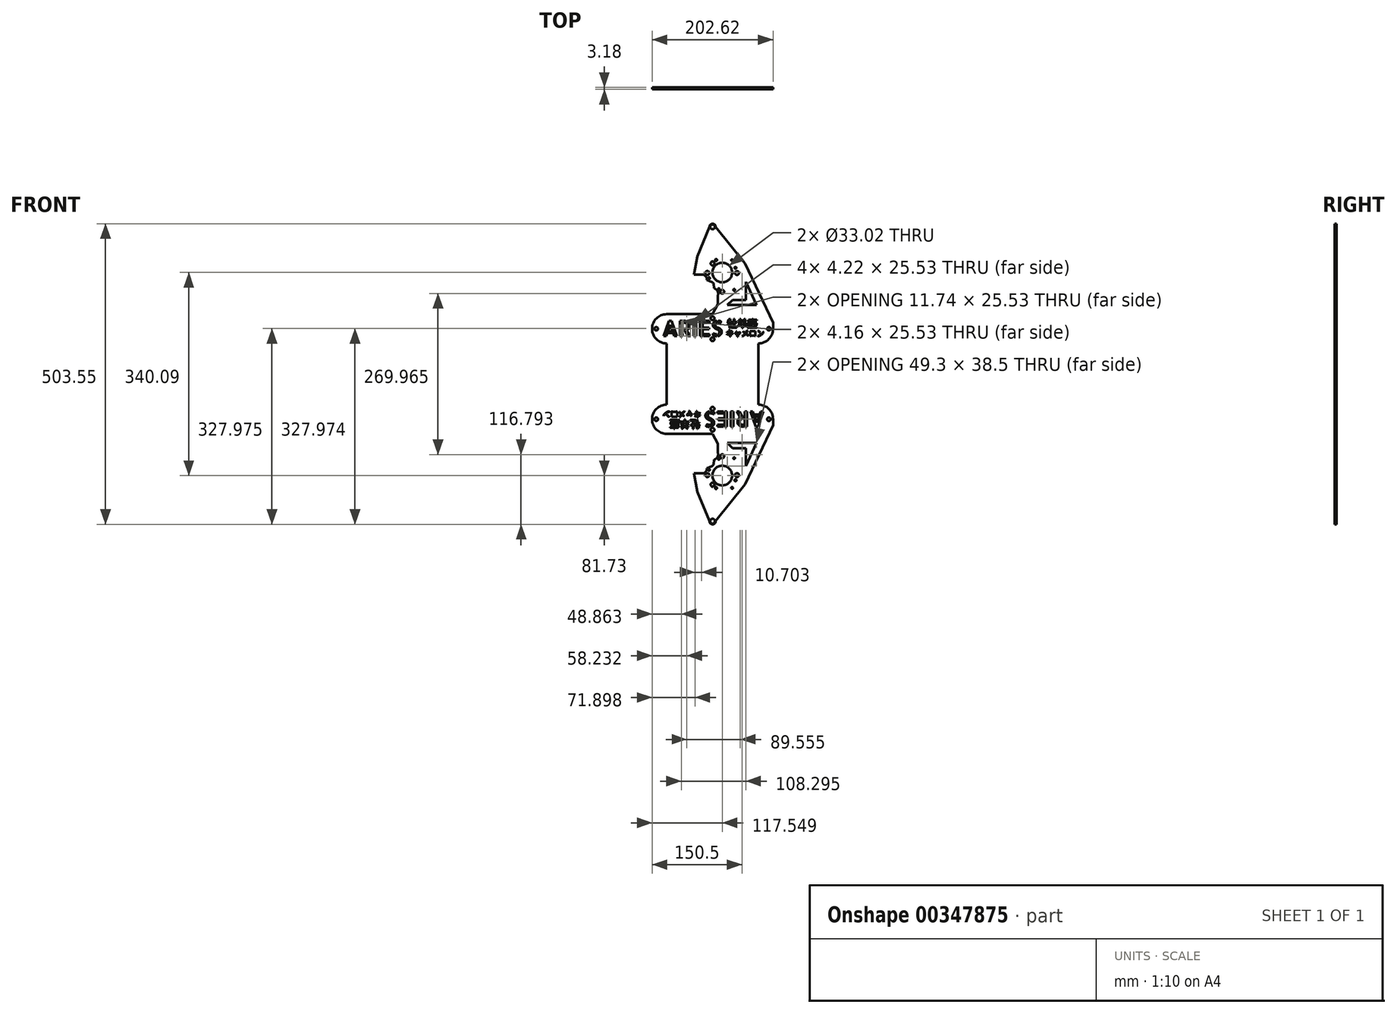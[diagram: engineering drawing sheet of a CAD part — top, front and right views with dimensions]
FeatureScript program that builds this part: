
annotation { "Feature Type Name" : "Feature", "Feature Type Description" : "" }
export const myFeature = defineFeature(function(context is Context, id is Id, definition is map)
    precondition{}
    {
        {
            var Q0;
            Q0=qCreatedBy(makeId("Front.planeOp"),FACE);
            var sketch = newSketch(context, id + "F0", { "sketchPlane" : qUnion([Q0])});
            skCircle(sketch, "E0", {"center": v(-4.64, -22.46) * mm, "radius": 3.17 * mm});
            skLineSegment(sketch, "E1", {"start": v(-4.64, -19.28) * mm, "end": v(-4.64, -15.53) * mm, "construction": true});
            skCircle(sketch, "E2", {"center": v(-4.64, -57.5) * mm, "radius": 3.18 * mm});
            skLineSegment(sketch, "E3", {"start": v(-4.64, -60.68) * mm, "end": v(-4.64, -19.28) * mm, "construction": true});
            skLineSegment(sketch, "E4", {"start": v(-4.64, -57.5) * mm, "end": v(-4.64, -64.5) * mm, "construction": true});
            skLineSegment(sketch, "E5", {"start": v(-81.45, -15.53) * mm, "end": v(-81.45, -29.5) * mm, "construction": true});
            skLineSegment(sketch, "E6", {"start": v(72.17, -15.47) * mm, "end": v(72.17, -29.44) * mm, "construction": true});
            skLineSegment(sketch, "E7", {"start": v(-4.64, -64.5) * mm, "end": v(72.17, -64.5) * mm, "construction": true});
            skLineSegment(sketch, "E8", {"start": v(72.17, -64.5) * mm, "end": v(72.17, -50.52) * mm, "construction": true});
            skLineSegment(sketch, "E9", {"start": v(-81.45, -64.5) * mm, "end": v(-4.64, -64.5) * mm, "construction": true});
            skLineSegment(sketch, "E10", {"start": v(72.17, -50.52) * mm, "end": v(72.17, -29.44) * mm, "construction": true});
            skLineSegment(sketch, "E11", {"start": v(-81.45, -50.52) * mm, "end": v(-81.45, -29.5) * mm, "construction": true});
            skPoint(sketch, "E12", {"position": v(-81.45, -40.01) * mm});
            skPoint(sketch, "E13", {"position": v(72.17, -39.98) * mm});
            skArc(sketch, "E14", {"start": v(-81.45, -64.5) * mm, "mid": v(-105.94, -40.01) * mm, "end": v(-81.45, -15.53) * mm});
            skLineSegment(sketch, "E15", {"start": v(82.71, -39.98) * mm, "end": v(96.68, -39.98) * mm, "construction": true});
            skLineSegment(sketch, "E16", {"start": v(-105.94, -40.01) * mm, "end": v(-92.02, -40.01) * mm, "construction": true});
            skCircle(sketch, "E17", {"center": v(-98.98, -40.01) * mm, "radius": 2.9 * mm});
            skCircle(sketch, "E18", {"center": v(89.7, -39.98) * mm, "radius": 2.9 * mm});
            skPoint(sketch, "E19", {"position": v(86.8, -39.98) * mm});
            skPoint(sketch, "E20", {"position": v(-96.08, -39.98) * mm});
            skCircle(sketch, "E21", {"center": v(-4.56, 69.29) * mm, "radius": 3.18 * mm});
            skLineSegment(sketch, "E22", {"start": v(-4.56, 66.11) * mm, "end": v(-4.56, 62.3) * mm, "construction": true});
            skCircle(sketch, "E23", {"center": v(-4.56, 130.79) * mm, "radius": 3.97 * mm});
            skArc(sketch, "E24", {"start": v(72.17, -64.5) * mm, "mid": v(89.5, -57.32) * mm, "end": v(96.68, -39.98) * mm});
            skLineSegment(sketch, "E25", {"start": v(-81.45, -64.5) * mm, "end": v(-81.45, -76.84) * mm});
            skLineSegment(sketch, "E26", {"start": v(-81.45, -76.84) * mm, "end": v(72.17, -76.84) * mm, "construction": true});
            skLineSegment(sketch, "E27", {"start": v(72.17, -76.84) * mm, "end": v(72.17, -64.5) * mm});
            skLineSegment(sketch, "E28", {"start": v(-19.49, 50.67) * mm, "end": v(-36, 50.68) * mm});
            skArc(sketch, "E29", {"start": v(-13.97, 42.17) * mm, "mid": v(-15.58, 47.16) * mm, "end": v(-19.49, 50.67) * mm});
            skLineSegment(sketch, "E30", {"start": v(-2.36, 27.9) * mm, "end": v(-2.9, 36.1) * mm});
            skLineSegment(sketch, "E31", {"start": v(-2.9, 36.1) * mm, "end": v(-5.4, 38.35) * mm});
            skLineSegment(sketch, "E32", {"start": v(-5.4, 38.35) * mm, "end": v(-13.97, 42.17) * mm});
            skCircle(sketch, "E33", {"center": v(-13.32, 53.53) * mm, "radius": 3.3 * mm});
            skCircle(sketch, "E34", {"center": v(-10.65, 44.71) * mm, "radius": 1.46 * mm});
            skCircle(sketch, "E35", {"center": v(11.54, 22) * mm, "radius": 3.3 * mm});
            skCircle(sketch, "E36", {"center": v(36.3, 53.5) * mm, "radius": 3.3 * mm});
            skCircle(sketch, "E37", {"center": v(31.58, 25.22) * mm, "radius": 1.47 * mm});
            skCircle(sketch, "E38", {"center": v(5.8, 26.2) * mm, "radius": 1.53 * mm});
            skCircle(sketch, "E39", {"center": v(1.14, 75.17) * mm, "radius": 1.7 * mm});
            skCircle(sketch, "E40", {"center": v(28.09, 75.01) * mm, "radius": 1.44 * mm});
            skCircle(sketch, "E41", {"center": v(-5.25, 71.7) * mm, "radius": 1.43 * mm});
            skCircle(sketch, "E42", {"center": v(11.6, 54.31) * mm, "radius": 16.51 * mm});
            skCircle(sketch, "E43", {"center": v(33.75, 62.23) * mm, "radius": 1.56 * mm});
            skLineSegment(sketch, "E44", {"start": v(4.29, 1.01) * mm, "end": v(-4.64, -15.53) * mm});
            skLineSegment(sketch, "E45", {"start": v(-4.64, -15.53) * mm, "end": v(-81.45, -15.53) * mm});
            skLineSegment(sketch, "E46", {"start": v(-9.81, 130.79) * mm, "end": v(-29.95, 81.4) * mm});
            skLineSegment(sketch, "E47", {"start": v(-4.64, -29.44) * mm, "end": v(-4.56, 115.55) * mm, "construction": true});
            skLineSegment(sketch, "E48", {"start": v(0.69, 130.79) * mm, "end": v(-9.81, 130.79) * mm, "construction": true});
            skArc(sketch, "E49", {"start": v(0.69, 130.79) * mm, "mid": v(-4.56, 136.04) * mm, "end": v(-9.81, 130.79) * mm});
            skLineSegment(sketch, "E50", {"start": v(-29.95, 81.4) * mm, "end": v(-36, 50.68) * mm});
            skLineSegment(sketch, "E51", {"start": v(0.69, 130.79) * mm, "end": v(49.8, 69.1) * mm});
            skLineSegment(sketch, "E52", {"start": v(49.8, 69.1) * mm, "end": v(96.68, -30.06) * mm});
            skText(sketch, "E53", { "text": "ARIES", "fontName": "AllertaStencil-Regular.ttf"});
            skText(sketch, "E54", { "text": "牡羊座", "fontName": "NotoSansCJKjp-Regular.otf"});
            skText(sketch, "E55", { "text": "キャメロン", "fontName": "NotoSansCJKjp-Regular.otf"});
            skLineSegment(sketch, "E56", {"start": v(72.17, -76.84) * mm, "end": v(72.17, -154.63) * mm});
            skLineSegment(sketch, "E57", {"start": v(72.17, -154.63) * mm, "end": v(-81.45, -154.63) * mm, "construction": true});
            skLineSegment(sketch, "E58", {"start": v(-81.45, -154.63) * mm, "end": v(-81.45, -76.84) * mm});
            skLineSegment(sketch, "E59", {"start": v(-81.45, -64.5) * mm, "end": v(-81.45, -15.53) * mm, "construction": true});
            skLineSegment(sketch, "E60", {"start": v(4.29, 16.25) * mm, "end": v(4.29, 1.01) * mm});
            skLineSegment(sketch, "E61", {"start": v(96.68, -39.98) * mm, "end": v(96.68, -30.06) * mm});
            skPoint(sketch, "E62", {"position": v(-4.64, 18.83) * mm});
            skArc(sketch, "E63", {"start": v(-2.36, 27.9) * mm, "mid": v(3.44, 23.54) * mm, "end": v(4.37, 16.35) * mm});
            skLineSegment(sketch, "E64", {"start": v(4.29, 16.25) * mm, "end": v(4.37, 16.35) * mm});
            skLineSegment(sketch, "E65", {"start": v(51, 38.5) * mm, "end": v(69.2, 0) * mm});
            skLineSegment(sketch, "E66", {"start": v(29.22, 8.37) * mm, "end": v(51, 8.37) * mm});
            skLineSegment(sketch, "E67", {"start": v(29.22, 8.37) * mm, "end": v(19.91, 0) * mm});
            skLineSegment(sketch, "E68", {"start": v(51, 8.37) * mm, "end": v(51, 38.5) * mm});
            skLineSegment(sketch, "E69", {"start": v(19.91, 0) * mm, "end": v(69.2, 0) * mm});
            skPoint(sketch, "E70", {"position": v(-81.45, -115.73) * mm});
            skPoint(sketch, "E71", {"position": v(72.17, -115.73) * mm});
            skLineSegment(sketch, "E72", {"start": v(-81.45, -115.73) * mm, "end": v(72.17, -115.73) * mm, "construction": true});
            skCircle(sketch, "E73.MirrorC", {"center": v(-4.56, -362.26) * mm, "radius": 3.97 * mm});
            skArc(sketch, "E74.MirrorCS", {"start": v(0.69, -362.26) * mm, "mid": v(-4.56, -367.5) * mm, "end": v(-9.81, -362.26) * mm});
            skLineSegment(sketch, "E75.MirrorCS", {"start": v(0.69, -362.26) * mm, "end": v(-9.81, -362.26) * mm, "construction": true});
            skLineSegment(sketch, "E76.MirrorCS", {"start": v(72.17, -166.98) * mm, "end": v(72.17, -180.95) * mm, "construction": true});
            skLineSegment(sketch, "E77.MirrorCS", {"start": v(-4.64, -212.19) * mm, "end": v(-4.64, -215.94) * mm, "construction": true});
            skCircle(sketch, "E78.MirrorC", {"center": v(-4.64, -209.01) * mm, "radius": 3.17 * mm});
            skLineSegment(sketch, "E79.MirrorCS", {"start": v(-4.64, -173.96) * mm, "end": v(-4.64, -166.98) * mm, "construction": true});
            skCircle(sketch, "E80.MirrorC", {"center": v(1.14, -306.64) * mm, "radius": 1.7 * mm});
            skLineSegment(sketch, "E81.MirrorCS", {"start": v(-2.36, -259.37) * mm, "end": v(-2.9, -267.57) * mm});
            skLineSegment(sketch, "E82.MirrorCS", {"start": v(82.71, -191.49) * mm, "end": v(96.68, -191.49) * mm, "construction": true});
            skLineSegment(sketch, "E83.MirrorCS", {"start": v(96.68, -191.49) * mm, "end": v(96.68, -201.41) * mm});
            skCircle(sketch, "E84.MirrorC", {"center": v(-5.25, -303.17) * mm, "radius": 1.43 * mm});
            skLineSegment(sketch, "E85.MirrorCS", {"start": v(72.17, -180.95) * mm, "end": v(72.17, -202.03) * mm, "construction": true});
            skCircle(sketch, "E86.MirrorC", {"center": v(5.8, -257.68) * mm, "radius": 1.53 * mm});
            skLineSegment(sketch, "E87.MirrorCS", {"start": v(-4.56, -297.58) * mm, "end": v(-4.56, -293.77) * mm, "construction": true});
            skCircle(sketch, "E88.MirrorC", {"center": v(-4.56, -300.76) * mm, "radius": 3.18 * mm});
            skCircle(sketch, "E89.MirrorC", {"center": v(89.7, -191.49) * mm, "radius": 2.9 * mm});
            skCircle(sketch, "E90.MirrorC", {"center": v(-4.64, -173.96) * mm, "radius": 3.18 * mm});
            skLineSegment(sketch, "E91.MirrorCS", {"start": v(4.29, -247.72) * mm, "end": v(4.37, -247.82) * mm});
            skLineSegment(sketch, "E92.MirrorCS", {"start": v(72.17, -216) * mm, "end": v(72.17, -202.03) * mm, "construction": true});
            skCircle(sketch, "E93.MirrorC", {"center": v(-10.65, -276.18) * mm, "radius": 1.46 * mm});
            skLineSegment(sketch, "E94.MirrorCS", {"start": v(-2.9, -267.57) * mm, "end": v(-5.4, -269.82) * mm});
            skLineSegment(sketch, "E95.MirrorCS", {"start": v(-81.45, -215.94) * mm, "end": v(-81.45, -201.97) * mm, "construction": true});
            skArc(sketch, "E96.MirrorCS", {"start": v(-13.97, -273.64) * mm, "mid": v(-15.58, -278.63) * mm, "end": v(-19.49, -282.14) * mm});
            skCircle(sketch, "E97.MirrorC", {"center": v(-13.32, -285) * mm, "radius": 3.3 * mm});
            skArc(sketch, "E98.MirrorCS", {"start": v(-2.36, -259.37) * mm, "mid": v(3.44, -255.01) * mm, "end": v(4.37, -247.82) * mm});
            skLineSegment(sketch, "E99.MirrorCS", {"start": v(4.29, -247.72) * mm, "end": v(4.29, -232.48) * mm});
            skLineSegment(sketch, "E100.MirrorCS", {"start": v(-81.45, -180.95) * mm, "end": v(-81.45, -201.97) * mm, "construction": true});
            skLineSegment(sketch, "E101.MirrorCS", {"start": v(19.91, -231.47) * mm, "end": v(69.2, -231.47) * mm});
            skLineSegment(sketch, "E102.MirrorCS", {"start": v(4.29, -232.48) * mm, "end": v(-4.64, -215.94) * mm});
            skLineSegment(sketch, "E103.MirrorCS", {"start": v(-19.49, -282.14) * mm, "end": v(-36, -282.15) * mm});
            skLineSegment(sketch, "E104.MirrorCS", {"start": v(29.22, -239.84) * mm, "end": v(19.91, -231.47) * mm});
            skCircle(sketch, "E105.MirrorC", {"center": v(11.54, -253.47) * mm, "radius": 3.3 * mm});
            skCircle(sketch, "E106.MirrorC", {"center": v(-98.98, -191.46) * mm, "radius": 2.9 * mm});
            skLineSegment(sketch, "E107.MirrorCS", {"start": v(-105.94, -191.46) * mm, "end": v(-92.02, -191.46) * mm, "construction": true});
            skLineSegment(sketch, "E108.MirrorCS", {"start": v(29.22, -239.84) * mm, "end": v(51, -239.84) * mm});
            skLineSegment(sketch, "E109.MirrorCS", {"start": v(-81.45, -166.98) * mm, "end": v(-81.45, -215.94) * mm, "construction": true});
            skLineSegment(sketch, "E110.MirrorCS", {"start": v(-5.4, -269.82) * mm, "end": v(-13.97, -273.64) * mm});
            skArc(sketch, "E111.MirrorCS", {"start": v(72.17, -166.98) * mm, "mid": v(89.5, -174.15) * mm, "end": v(96.68, -191.49) * mm});
            skCircle(sketch, "E112.MirrorC", {"center": v(28.09, -306.48) * mm, "radius": 1.44 * mm});
            skCircle(sketch, "E113.MirrorC", {"center": v(11.6, -285.78) * mm, "radius": 16.51 * mm});
            skCircle(sketch, "E114.MirrorC", {"center": v(31.58, -256.7) * mm, "radius": 1.47 * mm});
            skCircle(sketch, "E115.MirrorC", {"center": v(33.75, -293.7) * mm, "radius": 1.56 * mm});
            skCircle(sketch, "E116.MirrorC", {"center": v(36.3, -284.97) * mm, "radius": 3.3 * mm});
            skLineSegment(sketch, "E117.MirrorCS", {"start": v(-4.64, -170.79) * mm, "end": v(-4.64, -212.19) * mm, "construction": true});
            skLineSegment(sketch, "E118.MirrorCS", {"start": v(-9.81, -362.26) * mm, "end": v(-29.95, -312.87) * mm});
            skLineSegment(sketch, "E119.MirrorCS", {"start": v(-4.64, -202.03) * mm, "end": v(-4.56, -347.02) * mm, "construction": true});
            skArc(sketch, "E120.MirrorCS", {"start": v(-81.45, -166.98) * mm, "mid": v(-105.94, -191.46) * mm, "end": v(-81.45, -215.94) * mm});
            skLineSegment(sketch, "E121.MirrorCS", {"start": v(-81.45, -166.98) * mm, "end": v(-4.64, -166.98) * mm, "construction": true});
            skLineSegment(sketch, "E122.MirrorCS", {"start": v(49.8, -300.57) * mm, "end": v(96.68, -201.41) * mm});
            skLineSegment(sketch, "E123.MirrorCS", {"start": v(51, -239.84) * mm, "end": v(51, -269.96) * mm});
            skLineSegment(sketch, "E124.MirrorCS", {"start": v(-4.64, -166.98) * mm, "end": v(72.17, -166.98) * mm, "construction": true});
            skLineSegment(sketch, "E125.MirrorCS", {"start": v(0.69, -362.26) * mm, "end": v(49.8, -300.57) * mm});
            skLineSegment(sketch, "E126.MirrorCS", {"start": v(-29.95, -312.87) * mm, "end": v(-36, -282.15) * mm});
            skLineSegment(sketch, "E127.MirrorCS", {"start": v(-4.64, -215.94) * mm, "end": v(-81.45, -215.94) * mm});
            skPoint(sketch, "E128.MirrorP", {"position": v(86.8, -191.49) * mm});
            skPoint(sketch, "E129.MirrorP", {"position": v(-96.08, -191.49) * mm});
            skLineSegment(sketch, "E130.MirrorCS", {"start": v(51, -269.96) * mm, "end": v(69.2, -231.47) * mm});
            skLineSegment(sketch, "E131", {"start": v(-81.45, -166.98) * mm, "end": v(-81.45, -154.63) * mm});
            skLineSegment(sketch, "E132", {"start": v(72.17, -166.98) * mm, "end": v(72.17, -154.63) * mm});
            skText(sketch, "E133", { "text": "ARIES", "fontName": "AllertaStencil-Regular.ttf"});
            skText(sketch, "E134", { "text": "牡羊座", "fontName": "NotoSansCJKjp-Regular.otf"});
            skText(sketch, "E135", { "text": "キャメロン", "fontName": "NotoSansCJKjp-Regular.otf"});
            const initialGuessF0  = {"E53": [-0.08857, -0.0523, 1, 0, 0.02554], "E54": [0.02003, -0.03744, 1, 0, 0.01216], "E55": [0.01805, -0.0523, 1, 0, 0.00918], "E133": [0.08271, -0.1784, -1, 0, 0.02554], "E134": [-0.02588, -0.19326, -1, 0, 0.01216], "E135": [-0.0239, -0.1784, -1, 0, 0.00918]};
            skSetInitialGuess(sketch, initialGuessF0);
            skSolve(sketch);
        }
        {
            var Q0;
            Q0=makeQuery(id+"F0.imprint","IMPRINT",FACE,{"disambiguationData":[TD([[makeQuery(id+"F0.imprint","IMPRINT",EDGE,{"derivedFrom":sQuery(id+"F0.wireOp",EDGE,"E0")}),-1.0]])]});
            var Q1;
            Q1 = qSketchRegion(id + "F0", true);
            extrude(context, id + "F1", {"entities" : qUnion([Q0, Q1]), "depth" : 3.17 * mm});
        }
    });
